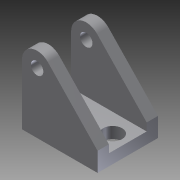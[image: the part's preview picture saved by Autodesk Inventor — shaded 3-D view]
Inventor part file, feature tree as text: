
AUTODESK INVENTOR PART (.ipt)
format: ipt  version: 2011 (Build 150239000, 239)  size: 136,192 bytes
history: native  units: in
note: dims shown in document units (in); Inventor stores cm internally (conversion verified against a paired STEP export)
features: extrude x5, sketch x5
ambient origin geometry x8: Origin, YZ Plane, XZ Plane, XY Plane, X Axis, Y Axis, Z Axis, Center Point
bodies: Solid1 (feature_tree)
feature tree (10):
  extrude  "Extrusion1"  Depth=1.5748in
  extrude  "Extrusion2"  Depth=0.315in
  extrude  "Extrusion3"  Depth=0.2598in
  extrude  "Extrusion4"  Depth=0.2362in
  extrude  "Extrusion5"  Depth=1.3386in TaperAngle=0.0deg
  sketch  "Sketch1"  dims[d0=1.5748in d1=1.5748in]
  sketch  "Sketch2"  dims[d2=0.3984in d3=0.315in]
  sketch  "Sketch3"  dims[d4=0.315in d5=0.2598in]
  sketch  "Sketch4"  dims[d6=1.2598in d7=0.0in d8=0.2362in]
  sketch  "Sketch5"  dims[d9=0.2362in d10=1.3386in d11=0.0in d12=0.3984in d13=1.3386in d14=0.0in d15=0.3937in d16=0.315in d17=0.3937in d18=1.3386in d19=0.0in d20=0.315in d21=1.3386in d22=0.0in]
